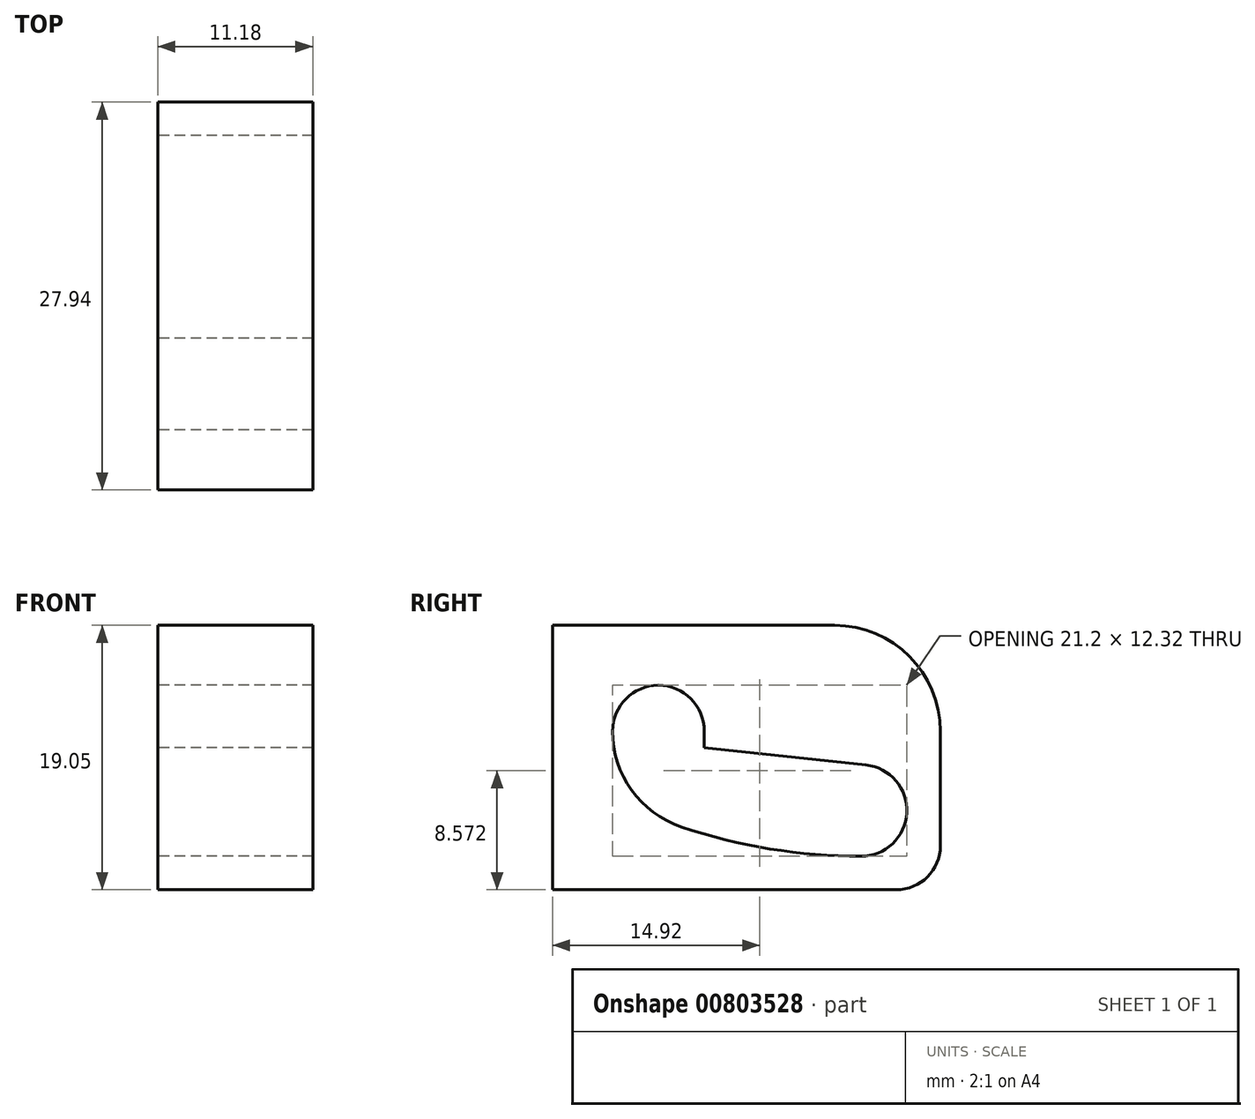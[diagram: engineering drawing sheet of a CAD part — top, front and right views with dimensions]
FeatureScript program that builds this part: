
annotation { "Feature Type Name" : "Feature", "Feature Type Description" : "" }
export const myFeature = defineFeature(function(context is Context, id is Id, definition is map)
    precondition{}
    {
        {
            var Q0;
            Q0=qCreatedBy(makeId("Right.planeOp"),FACE);
            var sketch = newSketch(context, id + "F0", { "sketchPlane" : qUnion([Q0])});
            skLineSegment(sketch, "E0", {"start": v(0, 0) * mm, "end": v(24.77, 0) * mm});
            skLineSegment(sketch, "E1", {"start": v(27.94, 3.18) * mm, "end": v(27.94, 11.43) * mm});
            skLineSegment(sketch, "E2", {"start": v(20.32, 19.05) * mm, "end": v(0, 19.05) * mm});
            skLineSegment(sketch, "E3", {"start": v(0, 19.05) * mm, "end": v(0, 0) * mm});
            skArc(sketch, "E4", {"start": v(10.92, 11.43) * mm, "mid": v(7.62, 14.73) * mm, "end": v(4.32, 11.43) * mm});
            skArc(sketch, "E5", {"start": v(22.23, 2.41) * mm, "mid": v(25.52, 5.54) * mm, "end": v(22.57, 9) * mm});
            skLineSegment(sketch, "E6", {"start": v(10.92, 11.43) * mm, "end": v(10.92, 10.22) * mm});
            skLineSegment(sketch, "E7", {"start": v(10.92, 10.22) * mm, "end": v(22.57, 9) * mm});
            skLineSegment(sketch, "E8", {"start": v(22.23, 2.41) * mm, "end": v(31.56, 2.41) * mm, "construction": true});
            skArc(sketch, "E9", {"start": v(9.28, 4.53) * mm, "mid": v(15.67, 2.95) * mm, "end": v(22.23, 2.41) * mm});
            skLineSegment(sketch, "E10", {"start": v(4.32, 11.43) * mm, "end": v(4.32, 16.7) * mm, "construction": true});
            skArc(sketch, "E11", {"start": v(4.32, 11.43) * mm, "mid": v(5.69, 7.18) * mm, "end": v(9.28, 4.53) * mm});
            skPoint(sketch, "E12.visualSharp", {"position": v(27.94, 19.05) * mm});
            skArc(sketch, "E12.filletArc", {"start": v(27.94, 11.43) * mm, "mid": v(25.7, 16.82) * mm, "end": v(20.32, 19.05) * mm});
            skPoint(sketch, "E13.visualSharp", {"position": v(27.94, 0) * mm});
            skArc(sketch, "E13.filletArc", {"start": v(24.77, 0) * mm, "mid": v(27.01, 0.93) * mm, "end": v(27.94, 3.18) * mm});
            skSolve(sketch);
        }
        {
            var Q0;
            Q0 = qSketchRegion(id + "F0", true);
            extrude(context, id + "F1", {"entities" : qUnion([Q0]), "endBound" : BoundingType.SYMMETRIC, "depth" : 11.18 * mm, "offsetDistance" : 25.4 * mm});
        }
    });
